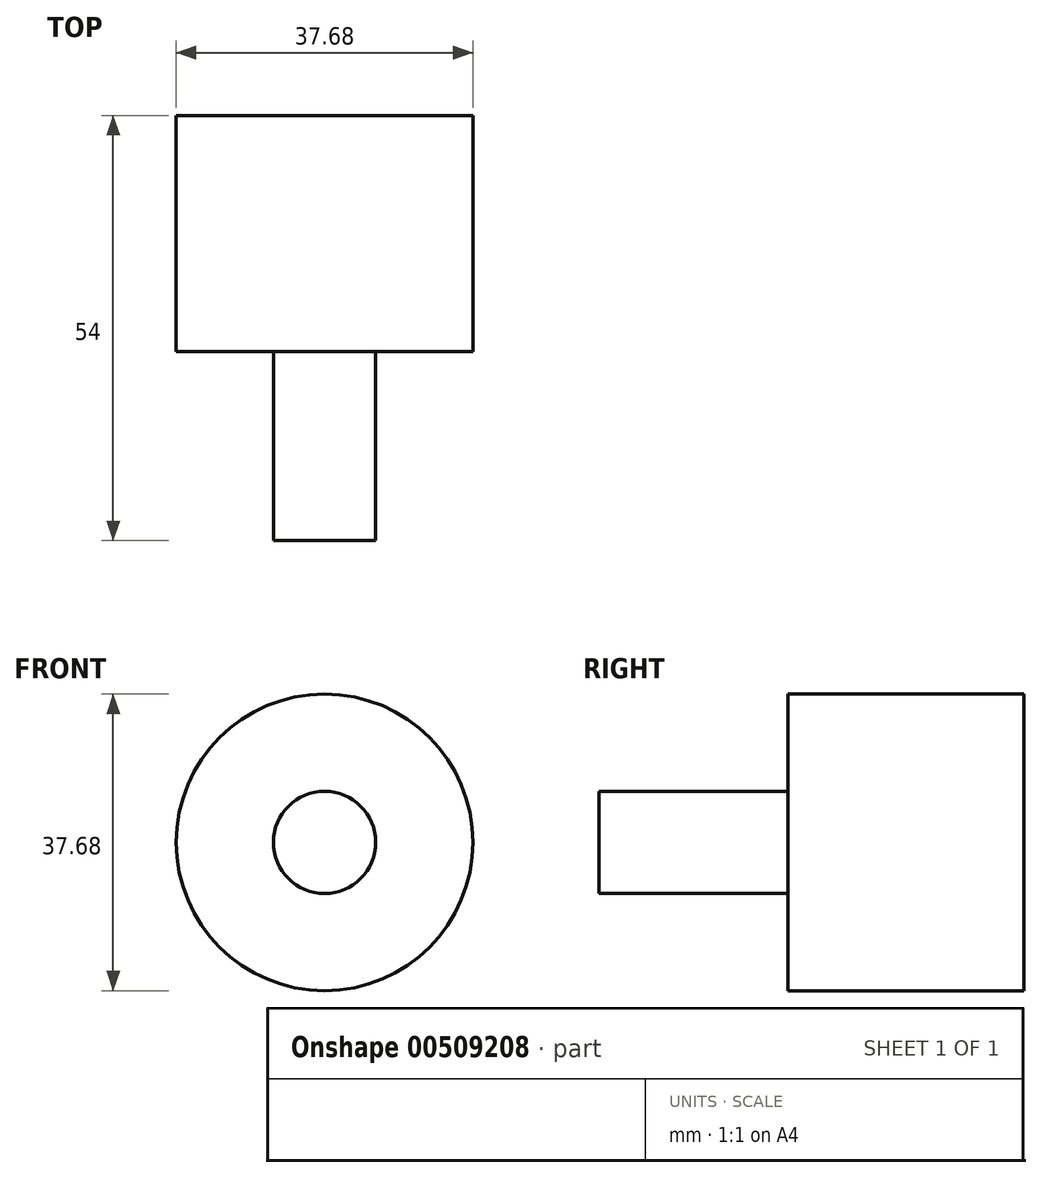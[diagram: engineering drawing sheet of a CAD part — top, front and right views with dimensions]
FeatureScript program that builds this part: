
annotation { "Feature Type Name" : "Feature", "Feature Type Description" : "" }
export const myFeature = defineFeature(function(context is Context, id is Id, definition is map)
    precondition{}
    {
        {
            var Q0;
            Q0=qCreatedBy(makeId("Front.planeOp"),FACE);
            var sketch = newSketch(context, id + "F0", { "sketchPlane" : qUnion([Q0])});
            skCircle(sketch, "E0", {"center": v(0, 0) * mm, "radius": 6.5 * mm});
            skSolve(sketch);
        }
        {
            var Q0;
            Q0=qSketchRegion(id+"F0",true);
            extrude(context, id + "F1", {"entities" : qUnion([Q0]), "depth" : 50 * mm});
        }
        {
            var Q0;
            Q0=makeQuery(id+"F1.opExtrude","CAP_FACE",FACE,{"disambiguationData":[OSD([sQuery(id+"F0.wireOp",EDGE,"E0")])],"isStart":true});
            var sketch = newSketch(context, id + "F2", { "sketchPlane" : qUnion([Q0])});
            skCircle(sketch, "E1", {"center": v(0, 0) * mm, "radius": 18.84 * mm});
            skSolve(sketch);
        }
        {
            var Q0;
            Q0=qSketchRegion(id+"F2",true);
            extrude(context, id + "F3", {"entities" : qUnion([Q0]), "operationType" : NewBodyOperationType.ADD, "depth" : 4 * mm, "hasSecondDirection" : true, "secondDirectionOppositeDirection" : true, "secondDirectionDepth" : 26 * mm});
        }
    });
